# Revit family: 32L-CR40-P-D
name_source: partatom
category: Lighting Fixtures
revit_build: Autodesk Revit MEP 2012 (Build: 20110309_2315(x64)
units: mm (PartAtom-declared; Revit-internal decimal feet)

## types (3) — shared parameters
Apparent Load = 0 VA
Assembly Code = D5020210
Color Filter = 16777215
Default Elevation = 4' - 0"
Description = Inde-Pendant 32 LED Cylinder & Ring Pendant Direct
Dimming Lamp Color Temperature Shift = <None>
Emit Shape Visible in Rendering = No
Emit from Circle Diameter = 0' - 6"
Glass = Hubbell - Glass
Lamp = LED
Manufacturer = Lite Control
Manufacturer Fax = 781-293-2849
Material = Hubbell Paint White
Model = 32L-CR40-P-D
Product Documentation Link = http://cdn.litecontrol.com
Product Page URL = http://www.litecontrol.com
Tilt Angle = 90.00°
URL = http://www.litecontrol.com
Voltage = 120 V

## per-type parameters (varying)
| type | Photometric Web File |
| ITL88482 | ITL88482-GONIOPHOTOMETRY.IES |
| ITL88488 | ITL88488-GONIOPHOTOMETRY.IES |
| ITL88490 | ITL88490-GONIOPHOTOMETRY.IES |

## geometry (parser evidence)
native form markers: Blend x2, Sweep x1
no freeform markers — native parametric forms only
